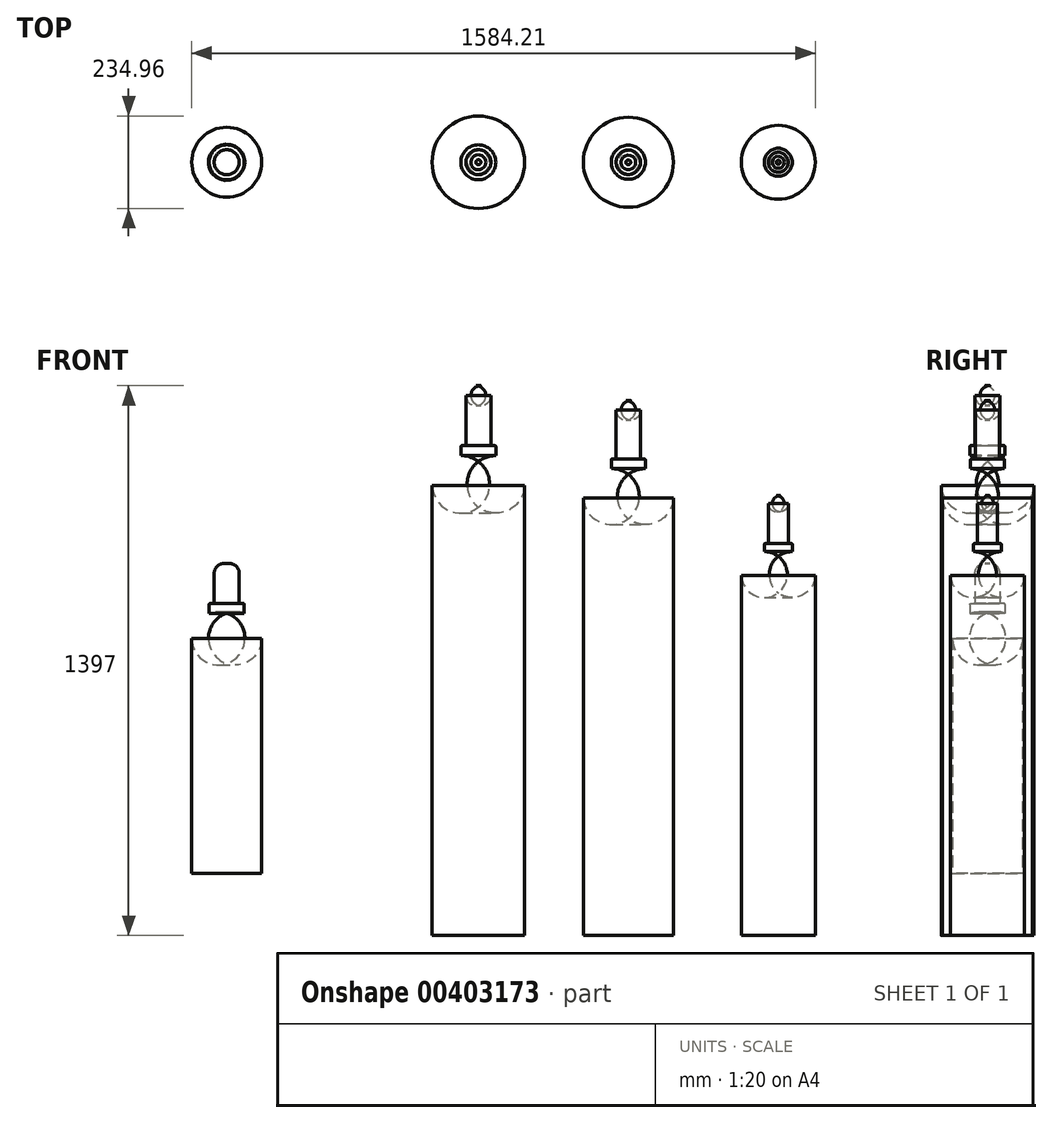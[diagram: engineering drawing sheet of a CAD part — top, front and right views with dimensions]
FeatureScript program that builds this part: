
annotation { "Feature Type Name" : "Feature", "Feature Type Description" : "" }
export const myFeature = defineFeature(function(context is Context, id is Id, definition is map)
    precondition{}
    {
        {
            var Q0;
            Q0=qCreatedBy(makeId("Front.planeOp"),FACE);
            var sketch = newSketch(context, id + "F0", { "sketchPlane" : qUnion([Q0])});
            skLineSegment(sketch, "E0", {"start": v(559.44, -35.4) * mm, "end": v(676.91, -35.4) * mm});
            skLineSegment(sketch, "E1", {"start": v(559.44, -35.4) * mm, "end": v(559.44, 1107.6) * mm});
            skLineSegment(sketch, "E2", {"start": v(676.91, -35.4) * mm, "end": v(676.91, 1361.6) * mm});
            skPoint(sketch, "E3", {"position": v(676.91, 1183.8) * mm});
            skLineSegment(sketch, "E4", {"start": v(632.46, 1183.8) * mm, "end": v(721.36, 1183.8) * mm, "construction": true});
            skArc(sketch, "E5", {"start": v(632.46, 1183.8) * mm, "mid": v(579.7, 1161.27) * mm, "end": v(559.44, 1107.6) * mm});
            skLineSegment(sketch, "E6", {"start": v(632.46, 1183.8) * mm, "end": v(632.46, 1206.39) * mm});
            skLineSegment(sketch, "E7", {"start": v(635.27, 1209.2) * mm, "end": v(645.16, 1209.2) * mm});
            skLineSegment(sketch, "E8", {"start": v(676.91, 1361.6) * mm, "end": v(670.56, 1361.6) * mm});
            skLineSegment(sketch, "E9", {"start": v(645.16, 1209.2) * mm, "end": v(645.16, 1336.2) * mm});
            skPoint(sketch, "E10.visualSharp", {"position": v(645.16, 1361.6) * mm});
            skArc(sketch, "E10.filletArc", {"start": v(670.56, 1361.6) * mm, "mid": v(652.6, 1354.15) * mm, "end": v(645.16, 1336.2) * mm});
            skPoint(sketch, "E11.visualSharp", {"position": v(632.46, 1209.2) * mm});
            skArc(sketch, "E11.filletArc", {"start": v(635.27, 1209.2) * mm, "mid": v(633.28, 1208.37) * mm, "end": v(632.46, 1206.39) * mm});
            skSolve(sketch);
        }
        {
            var Q0;
            Q0=makeQuery(id+"F0.imprint","IMPRINT",FACE,{"disambiguationData":[TD([[makeQuery(id+"F0.imprint","IMPRINT",EDGE,{"derivedFrom":sQuery(id+"F0.wireOp",EDGE,"E0")}),1.0]])]});
            var Q1;
            Q1=sQuery(id+"F0.wireOp",EDGE,"E2");
            revolve(context, id + "F1", {"entities" : qUnion([Q0]), "axis" : qUnion([Q1]), "revolveType" : RevolveType.FULL});
        }
        {
            var Q0;
            Q0=makeQuery(id+"F1.opRevolve","SWEPT_BODY",BODY,{"disambiguationData":[OSD([sQuery(id+"F0.wireOp",EDGE,"E0"),sQuery(id+"F0.wireOp",EDGE,"E1"),sQuery(id+"F0.wireOp",EDGE,"E2"),sQuery(id+"F0.wireOp",EDGE,"E5"),sQuery(id+"F0.wireOp",EDGE,"E6"),sQuery(id+"F0.wireOp",EDGE,"E7"),sQuery(id+"F0.wireOp",EDGE,"E8"),sQuery(id+"F0.wireOp",EDGE,"E9"),sQuery(id+"F0.wireOp",EDGE,"E10.filletArc"),sQuery(id+"F0.wireOp",EDGE,"E11.filletArc")])]});
            var Q1;
            Q1=sQuery(id+"F0.wireOp",VERTEX,"E2.start");
            transform(context, id + "F2", {"entities" : qUnion([Q0]), "transformType" : TransformType.SCALE_UNIFORMLY, "scale" : .97297, "scalePoint" : qUnion([Q1]), "makeCopy" : true});
        }
        {
            var Q0;
            Q0=makeQuery(id+"F2.opPattern","COPY",BODY,{"derivedFrom":makeQuery(id+"F1.opRevolve","SWEPT_BODY",BODY,{"disambiguationData":[OSD([sQuery(id+"F0.wireOp",EDGE,"E0"),sQuery(id+"F0.wireOp",EDGE,"E1"),sQuery(id+"F0.wireOp",EDGE,"E2"),sQuery(id+"F0.wireOp",EDGE,"E5"),sQuery(id+"F0.wireOp",EDGE,"E6"),sQuery(id+"F0.wireOp",EDGE,"E7"),sQuery(id+"F0.wireOp",EDGE,"E8"),sQuery(id+"F0.wireOp",EDGE,"E9"),sQuery(id+"F0.wireOp",EDGE,"E10.filletArc"),sQuery(id+"F0.wireOp",EDGE,"E11.filletArc")])]}),"instanceName":"1"});
            transform(context, id + "F3", {"entities" : qUnion([Q0]), "transformType" : TransformType.TRANSLATION_3D, "dx" : 381 * mm, "dy" : 0 * mm, "dz" : 0 * mm, "makeCopy" : false});
        }
        {
            var Q0;
            Q0=makeQuery(id+"F1.opRevolve","SWEPT_BODY",BODY,{"disambiguationData":[OSD([sQuery(id+"F0.wireOp",EDGE,"E0"),sQuery(id+"F0.wireOp",EDGE,"E1"),sQuery(id+"F0.wireOp",EDGE,"E2"),sQuery(id+"F0.wireOp",EDGE,"E5"),sQuery(id+"F0.wireOp",EDGE,"E6"),sQuery(id+"F0.wireOp",EDGE,"E7"),sQuery(id+"F0.wireOp",EDGE,"E8"),sQuery(id+"F0.wireOp",EDGE,"E9"),sQuery(id+"F0.wireOp",EDGE,"E10.filletArc"),sQuery(id+"F0.wireOp",EDGE,"E11.filletArc")])]});
            var Q1;
            Q1=sQuery(id+"F0.wireOp",VERTEX,"E2.start");
            transform(context, id + "F4", {"entities" : qUnion([Q0]), "transformType" : TransformType.SCALE_UNIFORMLY, "scale" : .8, "scalePoint" : qUnion([Q1]), "makeCopy" : true});
        }
        {
            var Q0;
            Q0=makeQuery(id+"F4.opPattern","COPY",BODY,{"derivedFrom":makeQuery(id+"F1.opRevolve","SWEPT_BODY",BODY,{"disambiguationData":[OSD([sQuery(id+"F0.wireOp",EDGE,"E0"),sQuery(id+"F0.wireOp",EDGE,"E1"),sQuery(id+"F0.wireOp",EDGE,"E2"),sQuery(id+"F0.wireOp",EDGE,"E5"),sQuery(id+"F0.wireOp",EDGE,"E6"),sQuery(id+"F0.wireOp",EDGE,"E7"),sQuery(id+"F0.wireOp",EDGE,"E8"),sQuery(id+"F0.wireOp",EDGE,"E9"),sQuery(id+"F0.wireOp",EDGE,"E10.filletArc"),sQuery(id+"F0.wireOp",EDGE,"E11.filletArc")])]}),"instanceName":"1"});
            transform(context, id + "F5", {"entities" : qUnion([Q0]), "transformType" : TransformType.TRANSLATION_3D, "dx" : 762 * mm, "dy" : 0 * mm, "dz" : 0 * mm, "makeCopy" : false});
        }
        {
            var Q0;
            Q0=qCreatedBy(makeId("Front.planeOp"),FACE);
            var sketch = newSketch(context, id + "F6", { "sketchPlane" : qUnion([Q0])});
            skLineSegment(sketch, "E12", {"start": v(-51.32, -1096.64) * mm, "end": v(37.58, -1096.64) * mm});
            skLineSegment(sketch, "E13", {"start": v(-51.32, -1096.64) * mm, "end": v(-51.32, -499.74) * mm});
            skLineSegment(sketch, "E14", {"start": v(37.58, -1096.64) * mm, "end": v(37.58, -309.24) * mm});
            skPoint(sketch, "E15", {"position": v(37.58, -436.24) * mm});
            skLineSegment(sketch, "E16", {"start": v(-6.87, -436.24) * mm, "end": v(82.03, -436.24) * mm, "construction": true});
            skLineSegment(sketch, "E17", {"start": v(-6.87, -436.24) * mm, "end": v(-6.87, -413.65) * mm});
            skLineSegment(sketch, "E18", {"start": v(-4.06, -410.84) * mm, "end": v(5.83, -410.84) * mm});
            skLineSegment(sketch, "E19", {"start": v(37.58, -309.24) * mm, "end": v(31.23, -309.24) * mm});
            skLineSegment(sketch, "E20", {"start": v(5.83, -410.84) * mm, "end": v(5.83, -334.64) * mm});
            skPoint(sketch, "E21.visualSharp", {"position": v(5.83, -309.24) * mm});
            skArc(sketch, "E21.filletArc", {"start": v(31.23, -309.24) * mm, "mid": v(13.27, -316.68) * mm, "end": v(5.83, -334.64) * mm});
            skPoint(sketch, "E22.visualSharp", {"position": v(-6.87, -410.84) * mm});
            skArc(sketch, "E22.filletArc", {"start": v(-4.06, -410.84) * mm, "mid": v(-6.05, -411.66) * mm, "end": v(-6.87, -413.65) * mm});
            skArc(sketch, "E23", {"start": v(-6.87, -436.24) * mm, "mid": v(-39.1, -460.98) * mm, "end": v(-51.32, -499.74) * mm});
            skSolve(sketch);
        }
        {
            var Q0;
            Q0=makeQuery(id+"F6.imprint","IMPRINT",FACE,{"disambiguationData":[TD([[makeQuery(id+"F6.imprint","IMPRINT",EDGE,{"derivedFrom":sQuery(id+"F6.wireOp",EDGE,"E12")}),1.0]])]});
            var Q1;
            Q1=sQuery(id+"F6.wireOp",EDGE,"E14");
            revolve(context, id + "F7", {"entities" : qUnion([Q0]), "axis" : qUnion([Q1]), "revolveType" : RevolveType.FULL});
        }
        {
            var Q0;
            Q0=makeQuery(id+"F7.opRevolve","SWEPT_BODY",BODY,{"disambiguationData":[OSD([sQuery(id+"F6.wireOp",EDGE,"E12"),sQuery(id+"F6.wireOp",EDGE,"E13"),sQuery(id+"F6.wireOp",EDGE,"E14"),sQuery(id+"F6.wireOp",EDGE,"E17"),sQuery(id+"F6.wireOp",EDGE,"E18"),sQuery(id+"F6.wireOp",EDGE,"E19"),sQuery(id+"F6.wireOp",EDGE,"E20"),sQuery(id+"F6.wireOp",EDGE,"E21.filletArc"),sQuery(id+"F6.wireOp",EDGE,"E22.filletArc"),sQuery(id+"F6.wireOp",EDGE,"E23")])]});
            var Q1;
            Q1=qCreatedBy(makeId("Origin.pointOp"),VERTEX);
            transform(context, id + "F8", {"entities" : qUnion([Q0]), "transformType" : TransformType.TRANSLATION_3D, "dx" : 0 * mm, "dy" : 0 * mm, "dz" : 1219.2 * mm, "makeCopy" : false});
        }
    });
